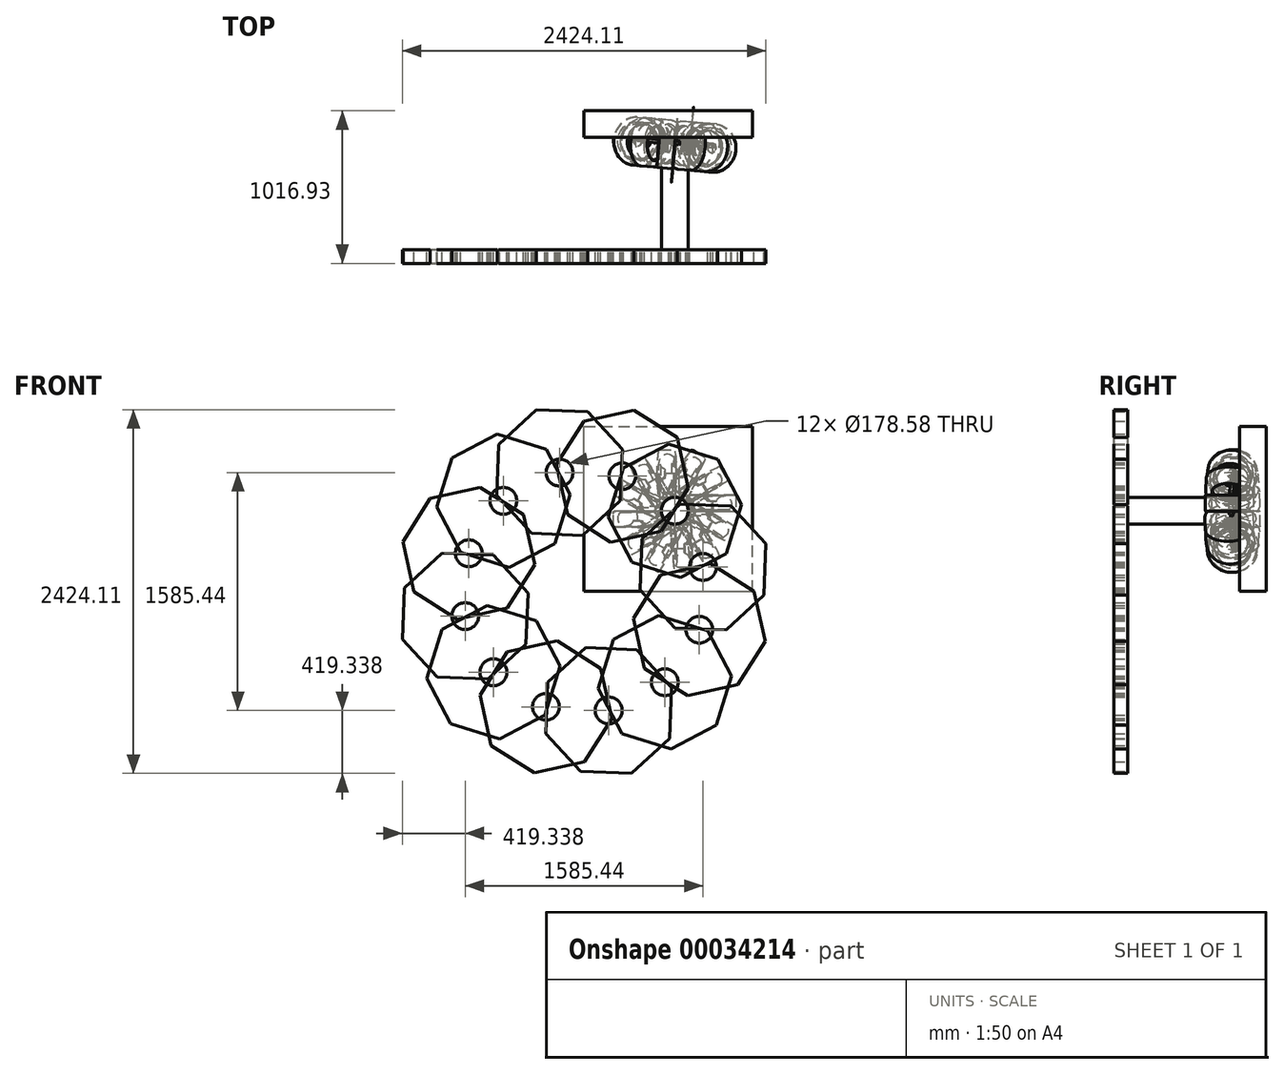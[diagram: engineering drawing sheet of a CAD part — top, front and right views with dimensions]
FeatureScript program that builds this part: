
annotation { "Feature Type Name" : "Feature", "Feature Type Description" : "" }
export const myFeature = defineFeature(function(context is Context, id is Id, definition is map)
    precondition{}
    {
        {
            var Q0;
            Q0=qCreatedBy(makeId("Front.planeOp"),FACE);
            var sketch = newSketch(context, id + "F0", { "sketchPlane" : qUnion([Q0])});
            skLineSegment(sketch, "E0", {"start": v(-105.22, 65.84) * mm, "end": v(-105.22, -42.5) * mm});
            skLineSegment(sketch, "E1", {"start": v(-105.22, 65.84) * mm, "end": v(55.41, 65.84) * mm});
            skLineSegment(sketch, "E2", {"start": v(55.41, 65.84) * mm, "end": v(55.41, -40.02) * mm});
            skLineSegment(sketch, "E3", {"start": v(55.41, -40.02) * mm, "end": v(-105.22, -42.5) * mm});
            skCircle(sketch, "E4", {"center": v(-24.9, 16.95) * mm, "radius": 52.61 * mm});
            skPoint(sketch, "E4.centerSnap0", {"position": v(-24.9, 65.84) * mm});
            skLineSegment(sketch, "E5.bottom", {"start": v(-105.22, 37.31) * mm, "end": v(-25.79, 37.31) * mm});
            skLineSegment(sketch, "E5.top", {"start": v(-105.22, 0) * mm, "end": v(-25.79, 0) * mm});
            skLineSegment(sketch, "E5.left", {"start": v(-105.22, 37.31) * mm, "end": v(-105.22, 0) * mm});
            skLineSegment(sketch, "E5.right", {"start": v(-25.79, 37.31) * mm, "end": v(-25.79, 0) * mm});
            skSolve(sketch);
        }
        {
            var Q0;
            {var subQ3=sQuery(id+"F0.wireOp",EDGE,"E0");var subQ5=sQuery(id+"F0.wireOp",EDGE,"E1");var subQ7=makeQuery(id+"F0.imprint","INTERSECT",VERTEX,{"derivedFrom":[subQ3,subQ5]});Q0=makeQuery(id+"F0.imprint","IMPRINT",FACE,{"disambiguationData":[TD([[makeQuery(id+"F0.imprint","IMPRINT",EDGE,{"disambiguationData":[TD([[subQ7,-1.0]])],"derivedFrom":subQ5}),-1.0]])]});}
            var Q1;
            {var subQ8=sQuery(id+"F0.wireOp",EDGE,"E2");Q1=makeQuery(id+"F0.imprint","IMPRINT",FACE,{"disambiguationData":[TD([[makeQuery(id+"F0.imprint","IMPRINT",EDGE,{"derivedFrom":subQ8}),-1.0]])]});}
            var Q2;
            {var subQ0=sQuery(id+"F0.wireOp",EDGE,"E5.left");Q2=makeQuery(id+"F0.imprint","IMPRINT",FACE,{"disambiguationData":[TD([[makeQuery(id+"F0.imprint","IMPRINT",EDGE,{"derivedFrom":subQ0}),1.0]])]});}
            var Q3;
            {var subQ3=sQuery(id+"F0.wireOp",EDGE,"E5.right");Q3=makeQuery(id+"F0.imprint","IMPRINT",FACE,{"disambiguationData":[TD([[makeQuery(id+"F0.imprint","IMPRINT",EDGE,{"derivedFrom":subQ3}),-1.0]])]});}
            extrude(context, id + "F1", {"entities" : qUnion([Q0, Q1, Q2, Q3]), "depth" : 25.4 * mm});
        }
        {
            var Q0;
            Q0=makeQuery(id+"F1.opExtrude","CAP_FACE",FACE,{"disambiguationData":[OSD([sQuery(id+"F0.wireOp",EDGE,"E0"),sQuery(id+"F0.wireOp",EDGE,"E1"),sQuery(id+"F0.wireOp",EDGE,"E2"),sQuery(id+"F0.wireOp",EDGE,"E3"),sQuery(id+"F0.wireOp",EDGE,"E4"),sQuery(id+"F0.wireOp",EDGE,"E5.bottom"),sQuery(id+"F0.wireOp",EDGE,"E5.top"),sQuery(id+"F0.wireOp",EDGE,"E5.left"),sQuery(id+"F0.wireOp",EDGE,"E5.right")])],"isStart":false});
            var sketch = newSketch(context, id + "F2", { "sketchPlane" : qUnion([Q0])});
            skLineSegment(sketch, "E6", {"start": v(-105.22, 65.84) * mm, "end": v(-105.22, -42.5) * mm});
            skSolve(sketch);
        }
        {
            var Q0;
            Q0=makeQuery(id+"F2.imprint","IMPRINT",FACE,{"disambiguationData":[TD([[makeQuery(id+"F2.imprint","IMPRINT",EDGE,{"derivedFrom":sQuery(id+"F2.wireOp",EDGE,"E6")}),1.0]])]});
            var Q1;
            Q1=sQuery(id+"F2.wireOp",EDGE,"E6");
            revolve(context, id + "F3", {"operationType" : NewBodyOperationType.ADD, "entities" : qUnion([Q0]), "axis" : qUnion([Q1]), "revolveType" : RevolveType.FULL});
        }
        {
            var Q0;
            Q0=makeQuery(id+"F1.opExtrude","SWEPT_FACE",FACE,{"disambiguationData":[OSD([sQuery(id+"F0.wireOp",EDGE,"E3")])]});
            extrude(context, id + "F4", {"entities" : qUnion([Q0]), "operationType" : NewBodyOperationType.ADD, "oppositeDirection" : true, "depth" : 136.07 * mm});
        }
        {
            var Q0;
            Q0=makeQuery(id+"F3.opRevolve","SWEPT_EDGE",EDGE,{"disambiguationData":[OSD([sQuery(id+"F0.wireOp",EDGE,"E2"),sQuery(id+"F0.wireOp",EDGE,"E3")])]});
            var Q1;
            Q1=makeQuery(id+"F3.opRevolve","SWEPT_EDGE",EDGE,{"disambiguationData":[OSD([sQuery(id+"F0.wireOp",EDGE,"E1"),sQuery(id+"F0.wireOp",EDGE,"E2")])]});
            fillet(context, id + "F5", {"entities" : qUnion([Q0, Q1]), "radius" : 5.08 * mm, "tangentPropagation" : true, "rho" : 0.5, "crossSection" : FilletCrossSection.CONIC, "allowEdgeOverflow" : false});
        }
        {
            var Q0;
            {var subQ0=sQuery(id+"F0.wireOp",EDGE,"E3");Q0=makeQuery(id+"F4.opExtrude","CAP_EDGE",EDGE,{"disambiguationData":[OSD([subQ0]),TDD([makeQuery(id+"F1.opExtrude","CAP_EDGE",EDGE,{"disambiguationData":[OSD([subQ0])],"isStart":true})])],"isStart":false});}
            var Q1;
            {var subQ0=sQuery(id+"F0.wireOp",EDGE,"E3");Q1=makeQuery(id+"F4.opExtrude","CAP_EDGE",EDGE,{"disambiguationData":[OSD([subQ0]),TDD([makeQuery(id+"F1.opExtrude","CAP_EDGE",EDGE,{"disambiguationData":[OSD([subQ0])],"isStart":false})])],"isStart":false});}
            var Q2;
            Q2=makeQuery(id+"F4.opExtrude","CAP_EDGE",EDGE,{"disambiguationData":[OSD([sQuery(id+"F0.wireOp",EDGE,"E2"),sQuery(id+"F0.wireOp",EDGE,"E3")])],"isStart":false});
            var Q3;
            Q3=makeQuery(id+"F4.opExtrude","CAP_EDGE",EDGE,{"disambiguationData":[OSD([sQuery(id+"F0.wireOp",EDGE,"E0"),sQuery(id+"F0.wireOp",EDGE,"E3")])],"isStart":false});
            var Q4;
            {var subQ0=sQuery(id+"F0.wireOp",EDGE,"E1");var subQ1=sQuery(id+"F0.wireOp",EDGE,"E4");var subQ2=makeQuery(id+"F0.imprint","INTERSECT",VERTEX,{"disambiguationData":[OD(0.0)],"derivedFrom":[subQ0,subQ1]});Q4=makeQuery(id+"F3.opRevolve","SWEPT_EDGE",EDGE,{"disambiguationData":[OSD([subQ0,subQ1]),TDD([makeQuery(id+"F2.imprint","INTERSECT",VERTEX,{"derivedFrom":[makeQuery(id+"F1.opExtrude","CAP_EDGE",EDGE,{"disambiguationData":[OSD([subQ0]),TDD([makeQuery(id+"F0.imprint","IMPRINT",EDGE,{"disambiguationData":[TD([[makeQuery(id+"F0.imprint","INTERSECT",VERTEX,{"derivedFrom":[sQuery(id+"F0.wireOp",EDGE,"E0"),subQ0]}),-1.0]])],"derivedFrom":subQ0})])],"isStart":false}),makeQuery(id+"F1.opExtrude","CAP_EDGE",EDGE,{"disambiguationData":[OSD([subQ1]),TDD([makeQuery(id+"F0.imprint","IMPRINT",EDGE,{"disambiguationData":[TD([[subQ2,-1.0]])],"derivedFrom":subQ1})])],"isStart":false})]})])]});}
            chamfer(context, id + "F6", {"entities" : qUnion([Q0, Q1, Q2, Q3, Q4]), "width" : 5.08 * mm, "tangentPropagation" : true});
        }
        {
            var Q0;
            {var subQ0=sQuery(id+"F0.wireOp",EDGE,"E1");var subQ1=makeQuery(id+"F0.imprint","IMPRINT",EDGE,{"disambiguationData":[TD([[makeQuery(id+"F0.imprint","INTERSECT",VERTEX,{"derivedFrom":[subQ0,sQuery(id+"F0.wireOp",EDGE,"E2")]}),1.0]])],"derivedFrom":subQ0});Q0=makeQuery(id+"F3.boolean.opBoolean","MERGE",FACE,{"derivedFrom":[makeQuery(id+"F1.opExtrude","SWEPT_FACE",FACE,{"disambiguationData":[OSD([subQ0]),TDD([subQ1])]}),makeQuery(id+"F3.opRevolve","SWEPT_FACE",FACE,{"disambiguationData":[OSD([subQ0]),TDD([makeQuery(id+"F2.imprint","IMPRINT",EDGE,{"derivedFrom":makeQuery(id+"F1.opExtrude","CAP_EDGE",EDGE,{"disambiguationData":[OSD([subQ0]),TDD([subQ1])],"isStart":false})})])]})]});}
            var sketch = newSketch(context, id + "F7", { "sketchPlane" : qUnion([Q0])});
            skLineSegment(sketch, "E7", {"start": v(139.09, -82.2) * mm, "end": v(199.77, 595.49) * mm});
            skSolve(sketch);
        }
        {
            var Q0;
            Q0=makeQuery(id+"F1.opExtrude","SWEPT_BODY",BODY,{"disambiguationData":[OSD([sQuery(id+"F0.wireOp",EDGE,"E0"),sQuery(id+"F0.wireOp",EDGE,"E1"),sQuery(id+"F0.wireOp",EDGE,"E2"),sQuery(id+"F0.wireOp",EDGE,"E3"),sQuery(id+"F0.wireOp",EDGE,"E4"),sQuery(id+"F0.wireOp",EDGE,"E5.bottom"),sQuery(id+"F0.wireOp",EDGE,"E5.top"),sQuery(id+"F0.wireOp",EDGE,"E5.left"),sQuery(id+"F0.wireOp",EDGE,"E5.right")])]});
            var Q1;
            Q1=sQuery(id+"F7.wireOp",EDGE,"E7");
            circularPattern(context, id + "F8", {"entities" : qUnion([Q0]), "axis" : qUnion([Q1]), "angle" : 30 * degree, "instanceCount" : 12});
        }
        {
            var Q0;
            Q0=qCreatedBy(makeId("Front.planeOp"),FACE);
            var sketch = newSketch(context, id + "F9", { "sketchPlane" : qUnion([Q0])});
            skLineSegment(sketch, "E8.bottom", {"start": v(-462.37, -470.53) * mm, "end": v(659.8, -470.53) * mm});
            skLineSegment(sketch, "E8.top", {"start": v(-462.37, 629.85) * mm, "end": v(659.8, 629.85) * mm});
            skLineSegment(sketch, "E8.left", {"start": v(-462.37, -470.53) * mm, "end": v(-462.37, 629.85) * mm});
            skLineSegment(sketch, "E8.right", {"start": v(659.8, -470.53) * mm, "end": v(659.8, 629.85) * mm});
            skSolve(sketch);
        }
        {
            var Q0;
            Q0=makeQuery(id+"F9.imprint","IMPRINT",FACE,{"disambiguationData":[TD([[makeQuery(id+"F9.imprint","IMPRINT",EDGE,{"derivedFrom":sQuery(id+"F9.wireOp",EDGE,"E8.bottom")}),1.0]])]});
            extrude(context, id + "F10", {"entities" : qUnion([Q0]), "oppositeDirection" : true, "depth" : 178.06 * mm});
        }
        {
            var Q0;
            Q0=makeQuery(id+"F10.opExtrude","CAP_FACE",FACE,{"disambiguationData":[OSD([sQuery(id+"F9.wireOp",EDGE,"E8.bottom"),sQuery(id+"F9.wireOp",EDGE,"E8.top"),sQuery(id+"F9.wireOp",EDGE,"E8.left"),sQuery(id+"F9.wireOp",EDGE,"E8.right")])],"isStart":true});
            var sketch = newSketch(context, id + "F11", { "sketchPlane" : qUnion([Q0])});
            skCircle(sketch, "E9", {"center": v(142.23, 67.7) * mm, "radius": 89.3 * mm});
            skSolve(sketch);
        }
        {
            var Q0;
            Q0=makeQuery(id+"F11.imprint","IMPRINT",FACE,{"disambiguationData":[TD([[makeQuery(id+"F11.imprint","IMPRINT",EDGE,{"derivedFrom":sQuery(id+"F11.wireOp",EDGE,"E9")}),1.0]])]});
            extrude(context, id + "F12", {"entities" : qUnion([Q0]), "depth" : 747.77 * mm});
        }
        {
            var Q0;
            Q0=makeQuery(id+"F12.opExtrude","CAP_FACE",FACE,{"disambiguationData":[OSD([sQuery(id+"F11.wireOp",EDGE,"E9")])],"isStart":false});
            var sketch = newSketch(context, id + "F13", { "sketchPlane" : qUnion([Q0])});
            skCircle(sketch, "E10.cCircle", {"center": v(142.23, 67.7) * mm, "radius": 412.67 * mm, "construction": true});
            skLineSegment(sketch, "E10.0", {"start": v(428.47, 410.6) * mm, "end": v(587.1, 107.76) * mm});
            skLineSegment(sketch, "E10.1", {"start": v(587.1, 107.76) * mm, "end": v(485.13, -218.55) * mm});
            skLineSegment(sketch, "E10.2", {"start": v(485.13, -218.55) * mm, "end": v(182.3, -377.17) * mm});
            skLineSegment(sketch, "E10.3", {"start": v(182.3, -377.17) * mm, "end": v(-144, -275.2) * mm});
            skLineSegment(sketch, "E10.4", {"start": v(-144, -275.2) * mm, "end": v(-302.63, 27.63) * mm});
            skLineSegment(sketch, "E10.5", {"start": v(-302.63, 27.63) * mm, "end": v(-200.66, 353.93) * mm});
            skLineSegment(sketch, "E10.6", {"start": v(-200.66, 353.93) * mm, "end": v(102.17, 512.56) * mm});
            skLineSegment(sketch, "E10.7", {"start": v(102.17, 512.56) * mm, "end": v(428.47, 410.6) * mm});
            skPoint(sketch, "E10.0.midPoint", {"position": v(507.78, 259.17) * mm});
            skSolve(sketch);
        }
        {
            var Q0;
            Q0=makeQuery(id+"F13.imprint","IMPRINT",FACE,{"disambiguationData":[TD([[makeQuery(id+"F13.imprint","IMPRINT",EDGE,{"derivedFrom":sQuery(id+"F13.wireOp",EDGE,"E10.0")}),-1.0]])]});
            extrude(context, id + "F14", {"entities" : qUnion([Q0]), "depth" : 91.1 * mm});
        }
        {
            var Q0;
            Q0=makeQuery(id+"F14.opExtrude","SWEPT_BODY",BODY,{"disambiguationData":[OSD([sQuery(id+"F11.wireOp",EDGE,"E9"),sQuery(id+"F13.wireOp",EDGE,"E10.0"),sQuery(id+"F13.wireOp",EDGE,"E10.1"),sQuery(id+"F13.wireOp",EDGE,"E10.2"),sQuery(id+"F13.wireOp",EDGE,"E10.3"),sQuery(id+"F13.wireOp",EDGE,"E10.4"),sQuery(id+"F13.wireOp",EDGE,"E10.5"),sQuery(id+"F13.wireOp",EDGE,"E10.6"),sQuery(id+"F13.wireOp",EDGE,"E10.7")])]});
            var Q1;
            Q1=makeQuery(id+"F10.opExtrude","SWEPT_EDGE",EDGE,{"disambiguationData":[OSD([sQuery(id+"F9.wireOp",EDGE,"E8.bottom"),sQuery(id+"F9.wireOp",EDGE,"E8.left")])]});
            circularPattern(context, id + "F15", {"entities" : qUnion([Q0]), "axis" : qUnion([Q1]), "angle" : 30 * degree, "instanceCount" : 12});
        }
    });
